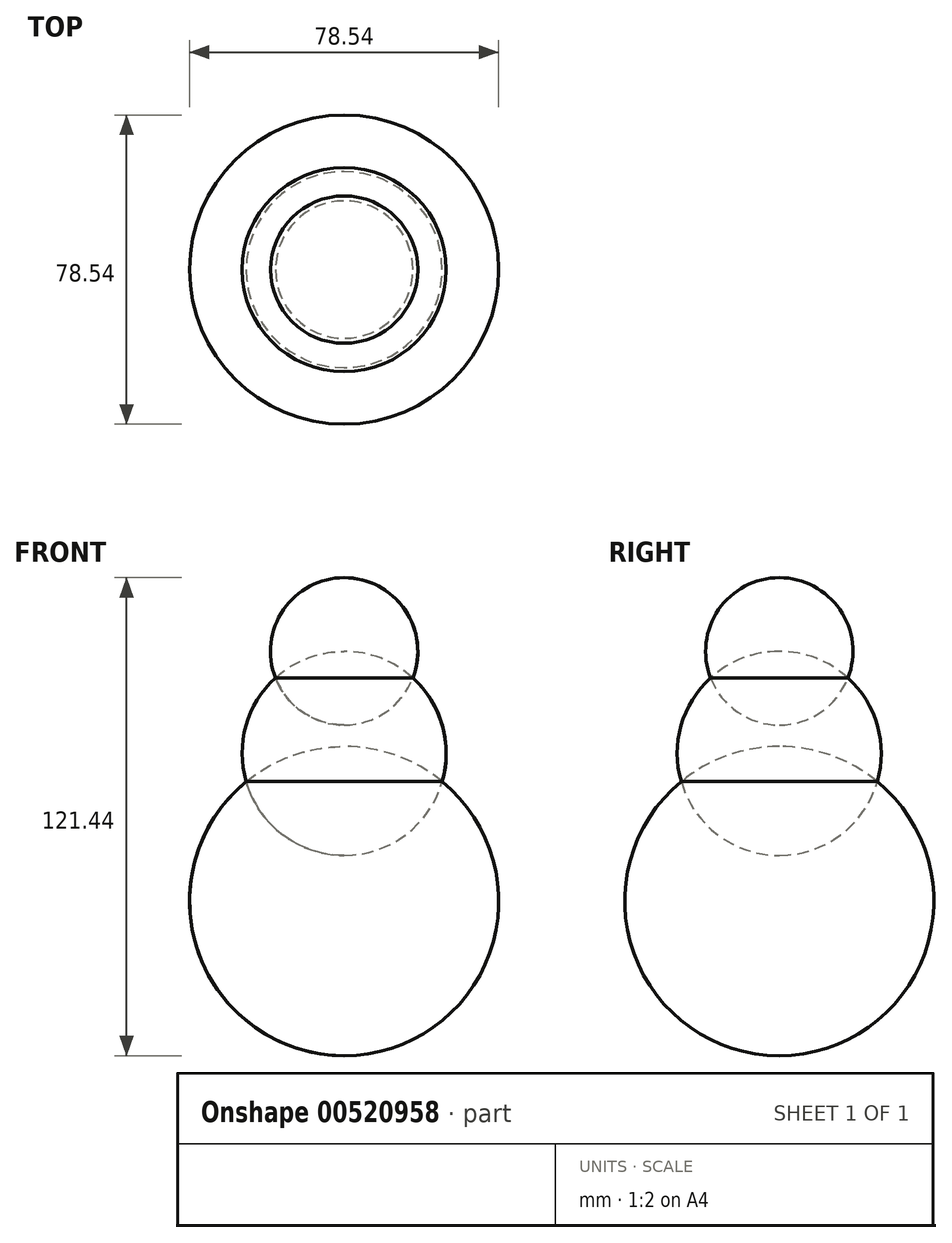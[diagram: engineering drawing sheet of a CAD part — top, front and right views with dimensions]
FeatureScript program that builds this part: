
annotation { "Feature Type Name" : "Feature", "Feature Type Description" : "" }
export const myFeature = defineFeature(function(context is Context, id is Id, definition is map)
    precondition{}
    {
        {
            var Q0;
            Q0=qCreatedBy(makeId("Front.planeOp"),FACE);
            var sketch = newSketch(context, id + "F0", { "sketchPlane" : qUnion([Q0])});
            skLineSegment(sketch, "E0", {"start": v(0, 65.7) * mm, "end": v(0, -76.8) * mm});
            skCircle(sketch, "E1", {"center": v(0, -37.53) * mm, "radius": 39.27 * mm});
            skCircle(sketch, "E2", {"center": v(0, 0) * mm, "radius": 25.93 * mm});
            skCircle(sketch, "E3", {"center": v(0, 25.93) * mm, "radius": 18.71 * mm});
            skSolve(sketch);
        }
        {
            var Q0;
            {var subQ0=sQuery(id+"F0.wireOp",EDGE,"E3");var subQ1=sQuery(id+"F0.wireOp",EDGE,"E0");var subQ2=makeQuery(id+"F0.imprint","INTERSECT",VERTEX,{"disambiguationData":[OD(0.0)],"derivedFrom":[subQ1,subQ0]});Q0=makeQuery(id+"F0.imprint","IMPRINT",FACE,{"disambiguationData":[TD([[makeQuery(id+"F0.imprint","IMPRINT",EDGE,{"disambiguationData":[TD([[subQ2,-1.0]])],"derivedFrom":subQ1}),-1.0]])]});}
            var Q1;
            {var subQ0=sQuery(id+"F0.wireOp",EDGE,"E3");var subQ1=sQuery(id+"F0.wireOp",EDGE,"E0");var subQ2=makeQuery(id+"F0.imprint","INTERSECT",VERTEX,{"disambiguationData":[OD(1.0)],"derivedFrom":[subQ1,subQ0]});Q1=makeQuery(id+"F0.imprint","IMPRINT",FACE,{"disambiguationData":[TD([[makeQuery(id+"F0.imprint","IMPRINT",EDGE,{"disambiguationData":[TD([[subQ2,-1.0]])],"derivedFrom":subQ1}),-1.0]])]});}
            var Q2;
            {var subQ0=sQuery(id+"F0.wireOp",EDGE,"E1");var subQ1=sQuery(id+"F0.wireOp",EDGE,"E0");var subQ2=makeQuery(id+"F0.imprint","INTERSECT",VERTEX,{"disambiguationData":[OD(0.0)],"derivedFrom":[subQ1,subQ0]});Q2=makeQuery(id+"F0.imprint","IMPRINT",FACE,{"disambiguationData":[TD([[makeQuery(id+"F0.imprint","IMPRINT",EDGE,{"disambiguationData":[TD([[subQ2,1.0]])],"derivedFrom":subQ1}),-1.0]])]});}
            var Q3;
            {var subQ0=sQuery(id+"F0.wireOp",EDGE,"E1");var subQ1=sQuery(id+"F0.wireOp",EDGE,"E0");var subQ2=makeQuery(id+"F0.imprint","INTERSECT",VERTEX,{"disambiguationData":[OD(1.0)],"derivedFrom":[subQ1,subQ0]});Q3=makeQuery(id+"F0.imprint","IMPRINT",FACE,{"disambiguationData":[TD([[makeQuery(id+"F0.imprint","IMPRINT",EDGE,{"disambiguationData":[TD([[subQ2,-1.0]])],"derivedFrom":subQ1}),-1.0]])]});}
            var Q4;
            {var subQ0=sQuery(id+"F0.wireOp",EDGE,"E2");var subQ1=sQuery(id+"F0.wireOp",EDGE,"E0");var subQ2=makeQuery(id+"F0.imprint","INTERSECT",VERTEX,{"disambiguationData":[OD(0.0)],"derivedFrom":[subQ1,subQ0]});Q4=makeQuery(id+"F0.imprint","IMPRINT",FACE,{"disambiguationData":[TD([[makeQuery(id+"F0.imprint","IMPRINT",EDGE,{"disambiguationData":[TD([[subQ2,-1.0]])],"derivedFrom":subQ1}),-1.0]])]});}
            var Q5;
            Q5=sQuery(id+"F0.wireOp",EDGE,"E0");
            revolve(context, id + "F1", {"entities" : qUnion([Q0, Q1, Q2, Q3, Q4]), "axis" : qUnion([Q5]), "revolveType" : RevolveType.FULL});
        }
    });
